# Revit family: Угловой запорно-регулирующий вентиль
name_source: partatom
category: Арматура трубопроводов
units: mm (PartAtom-declared; Revit-internal decimal feet)

## family parameters
Всегда вертикально = Нет
Заголовок OmniClass = Non-Return Valves for Liquid Services
На основе рабочей плоскости = Нет
Номер OmniClass = 23.65.55.14.21
Общий = Да
При загрузке вырезать с полостями = Нет
Размер круглого соединителя = Использовать диаметр
Тип детали = Клапан - Вставляется

## types (2) — shared parameters
ADSK_Единица измерения = шт.
ADSK_Завод-изготовитель = Weser
ADSK_Наименование краткое = Термостатический вентиль
URL = https://www.weser.ru
Высота крышки = 36 мм
Диаметр крышки = 39 мм
Длина адаптера = 8 мм
Длина корпуса = 82 мм
Материал клапана = Латунь
Толщина крышки = 12 мм
zero-valued in all types: Коэффициент K, Отметка по умолчанию

## per-type parameters (varying)
| type | ADSK_Диаметр условный | ADSK_Код изделия | ADSK_Наименование | Диаметр адаптера | Диаметр корпуса |
| Dn15 | 15 мм | 820220 | Угловой запорно-регулирующий вентиль Dn15 | 18 мм | 11 мм |
| Dn20 | 20 мм | 820230 | Угловой запорно-регулирующий вентиль Dn20 | 24 мм | 14 мм |
